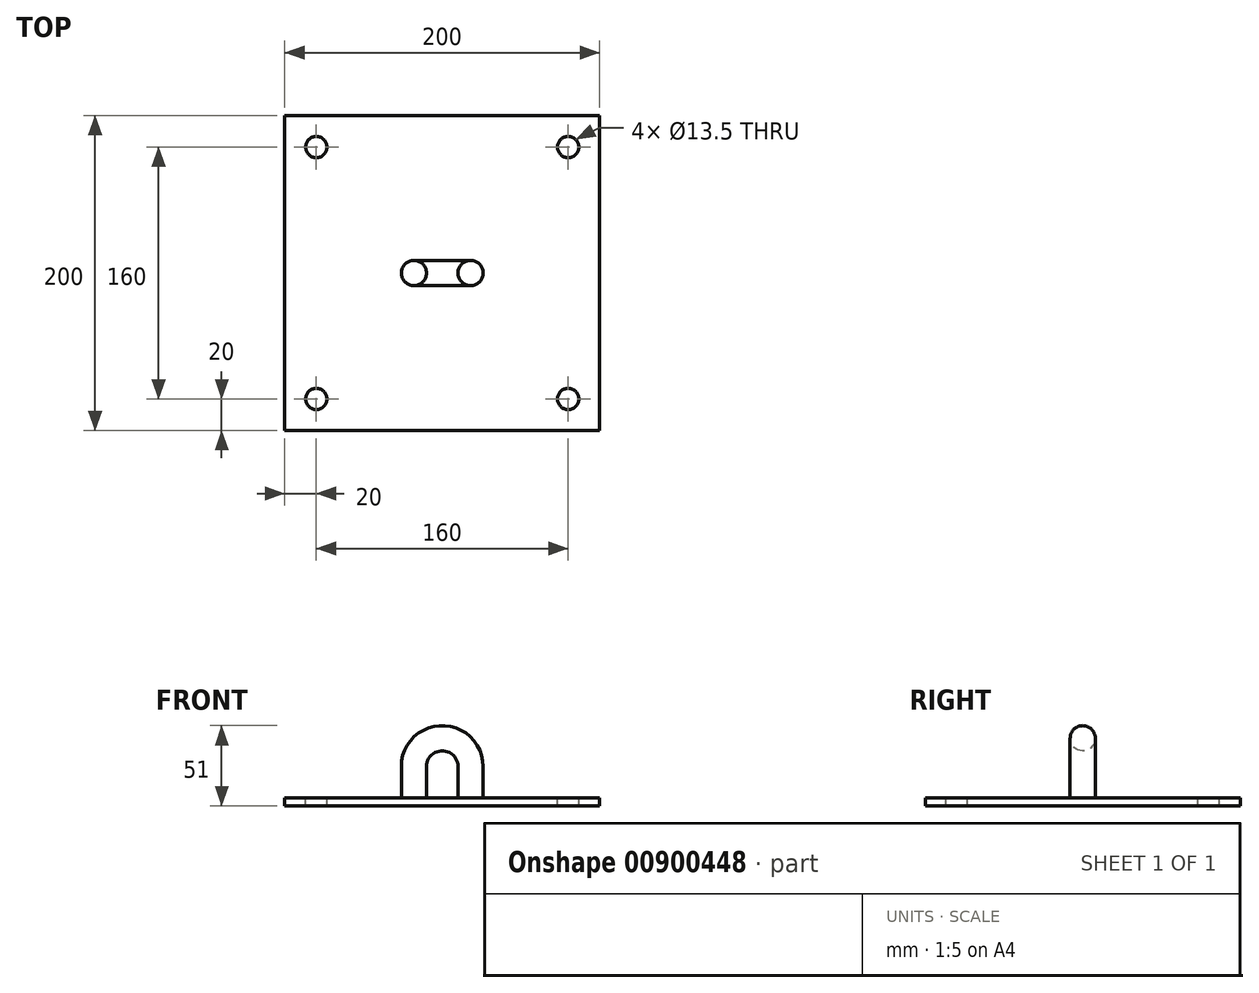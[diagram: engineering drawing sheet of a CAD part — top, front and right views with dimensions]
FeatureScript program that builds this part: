
annotation { "Feature Type Name" : "Feature", "Feature Type Description" : "" }
export const myFeature = defineFeature(function(context is Context, id is Id, definition is map)
    precondition{}
    {
        {
            var Q0;
            Q0=qCreatedBy(makeId("Top.planeOp"),FACE);
            var sketch = newSketch(context, id + "F0", { "sketchPlane" : qUnion([Q0])});
            skLineSegment(sketch, "E0.bottom", {"start": v(0, 0) * mm, "end": v(200, 0) * mm});
            skLineSegment(sketch, "E0.top", {"start": v(0, 200) * mm, "end": v(200, 200) * mm});
            skLineSegment(sketch, "E0.left", {"start": v(0, 0) * mm, "end": v(0, 200) * mm});
            skLineSegment(sketch, "E0.right", {"start": v(200, 0) * mm, "end": v(200, 200) * mm});
            skSolve(sketch);
        }
        {
            var Q0;
            Q0=makeQuery(id+"F0.imprint","IMPRINT",FACE,{"disambiguationData":[TD([[makeQuery(id+"F0.imprint","IMPRINT",EDGE,{"derivedFrom":sQuery(id+"F0.wireOp",EDGE,"E0.bottom")}),1.0]])]});
            extrude(context, id + "F1", {"entities" : qUnion([Q0]), "depth" : 5 * mm, "offsetDistance" : 25 * mm});
        }
        {
            var Q0;
            Q0=makeQuery(id+"F1.opExtrude","CAP_FACE",FACE,{"disambiguationData":[OSD([sQuery(id+"F0.wireOp",EDGE,"E0.bottom"),sQuery(id+"F0.wireOp",EDGE,"E0.top"),sQuery(id+"F0.wireOp",EDGE,"E0.left"),sQuery(id+"F0.wireOp",EDGE,"E0.right")])],"isStart":true});
            var sketch = newSketch(context, id + "F2", { "sketchPlane" : qUnion([Q0])});
            skPoint(sketch, "E1", {"position": v(20, -20) * mm});
            skPoint(sketch, "E2", {"position": v(180, -20) * mm});
            skPoint(sketch, "E3", {"position": v(20, -180) * mm});
            skPoint(sketch, "E4", {"position": v(180, -180) * mm});
            skSolve(sketch);
        }
        {
            var Q0;
            Q0=sQuery(id+"F2.wireOp",VERTEX,"E1");
            var Q1;
            Q1=sQuery(id+"F2.wireOp",VERTEX,"E2");
            var Q2;
            Q2=sQuery(id+"F2.wireOp",VERTEX,"E3");
            var Q3;
            Q3=sQuery(id+"F2.wireOp",VERTEX,"E4");
            var Q4;
            Q4=makeQuery(id+"F1.opExtrude","SWEPT_BODY",BODY,{"disambiguationData":[OSD([sQuery(id+"F0.wireOp",EDGE,"E0.bottom"),sQuery(id+"F0.wireOp",EDGE,"E0.top"),sQuery(id+"F0.wireOp",EDGE,"E0.left"),sQuery(id+"F0.wireOp",EDGE,"E0.right")])]});
            hole(context, id + "F3", {"style" : HoleStyle.SIMPLE, "endStyle" : HoleEndStyle.THROUGH, "standardTappedOrClearance" : lookupTablePath({ "fit" : "Normal", "standard" : "ISO", "size" : "M12", "type" : "Clearance" }), "standardBlindInLast" : lookupTablePath({ "fit" : "Normal", "standard" : "ISO", "size" : "M12", "type" : "Clearance" }), "holeDiameter" : 13.5 * mm, "majorDiameter" : 5 * mm, "isTappedThrough" : true, "tappedDepth" : 12 * mm, "tapClearance" : 3, "locations" : qUnion([Q0, Q1, Q2, Q3]), "scope" : qUnion([Q4])});
        }
        {
            var Q0;
            Q0=qCreatedBy(makeId("Front.planeOp"),FACE);
            cPlane(context, id + "F4", {"entities" : qUnion([Q0]), "cplaneType" : CPlaneType.OFFSET, "offset" : 100 * mm, "oppositeDirection" : true, "width" : 150 * mm, "height" : 150 * mm});
        }
        {
            var Q0;
            Q0=makeQuery(id+"F1.opExtrude","CAP_FACE",FACE,{"disambiguationData":[OSD([sQuery(id+"F0.wireOp",EDGE,"E0.bottom"),sQuery(id+"F0.wireOp",EDGE,"E0.top"),sQuery(id+"F0.wireOp",EDGE,"E0.left"),sQuery(id+"F0.wireOp",EDGE,"E0.right")])],"isStart":false});
            var sketch = newSketch(context, id + "F5", { "sketchPlane" : qUnion([Q0])});
            skCircle(sketch, "E5", {"center": v(118, 100) * mm, "radius": 8 * mm});
            skSolve(sketch);
        }
        {
            var Q0;
            Q0=makeQuery(id+"F5.imprint","IMPRINT",FACE,{"disambiguationData":[TD([[makeQuery(id+"F5.imprint","IMPRINT",EDGE,{"derivedFrom":sQuery(id+"F5.wireOp",EDGE,"E5")}),-1.0]])]});
            var sketch = newSketch(context, id + "F6", { "sketchPlane" : qUnion([Q0])});
            skCircle(sketch, "E6", {"center": v(82, 100) * mm, "radius": 6 * mm});
            skSolve(sketch);
        }
        {
            var Q0;
            Q0=qCreatedBy(id+"F4.planeOp",FACE);
            var sketch = newSketch(context, id + "F7", { "sketchPlane" : qUnion([Q0])});
            skLineSegment(sketch, "E7", {"start": v(118, 5) * mm, "end": v(118, 25) * mm});
            skLineSegment(sketch, "E8", {"start": v(82, 5) * mm, "end": v(82, 25) * mm});
            skArc(sketch, "E9", {"start": v(118, 25) * mm, "mid": v(100, 43) * mm, "end": v(82, 25) * mm});
            skSolve(sketch);
        }
        {
            var Q0;
            Q0 = qSketchRegion(id + "F5", true);
            var Q1;
            Q1 = qConstructionFilter(qBodyType(qCreatedBy(id + "F7" ,EDGE), BodyType.WIRE), ConstructionObject.NO);
            sweep(context, id + "F8", {"operationType" : NewBodyOperationType.ADD, "profiles" : qUnion([Q0]), "path" : qUnion([Q1])});
        }
    });
